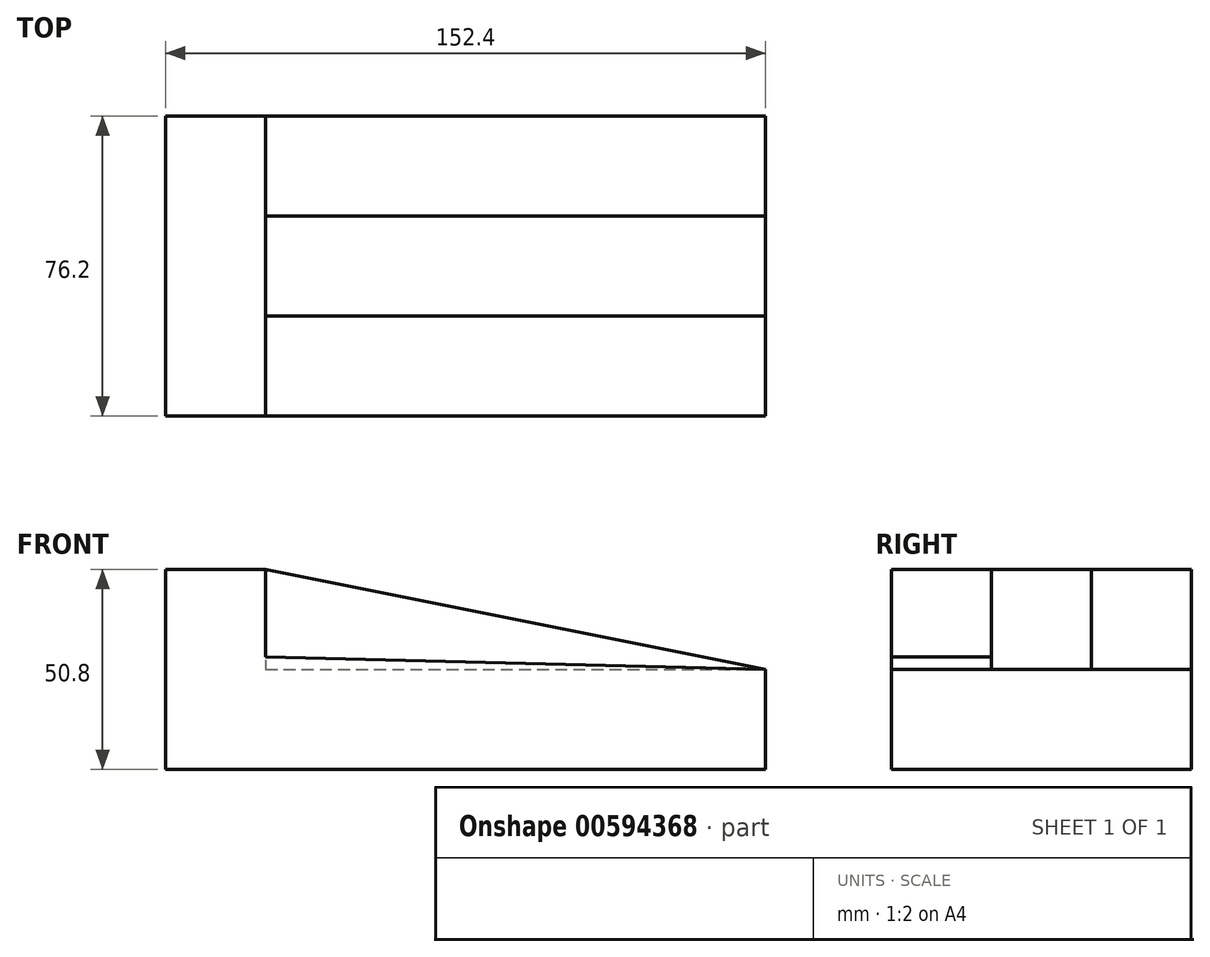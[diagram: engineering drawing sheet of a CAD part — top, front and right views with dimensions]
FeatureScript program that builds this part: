
annotation { "Feature Type Name" : "Feature", "Feature Type Description" : "" }
export const myFeature = defineFeature(function(context is Context, id is Id, definition is map)
    precondition{}
    {
        {
            var Q0;
            Q0=qCreatedBy(makeId("Front.planeOp"),FACE);
            var sketch = newSketch(context, id + "F0", { "sketchPlane" : qUnion([Q0])});
            skLineSegment(sketch, "E0", {"start": v(0, 0) * mm, "end": v(0, 50.8) * mm});
            skLineSegment(sketch, "E1", {"start": v(0, 50.8) * mm, "end": v(25.4, 50.8) * mm});
            skLineSegment(sketch, "E2", {"start": v(25.4, 50.8) * mm, "end": v(25.4, 25.4) * mm});
            skLineSegment(sketch, "E3", {"start": v(25.4, 25.4) * mm, "end": v(152.4, 25.4) * mm});
            skLineSegment(sketch, "E4", {"start": v(152.4, 25.4) * mm, "end": v(152.4, 0) * mm});
            skLineSegment(sketch, "E5", {"start": v(152.4, 0) * mm, "end": v(0, 0) * mm});
            skSolve(sketch);
        }
        {
            var Q0;
            Q0=makeQuery(id+"F0.imprint","IMPRINT",FACE,{"disambiguationData":[TD([[makeQuery(id+"F0.imprint","IMPRINT",EDGE,{"derivedFrom":sQuery(id+"F0.wireOp",EDGE,"E0")}),-1.0]])]});
            extrude(context, id + "F1", {"entities" : qUnion([Q0]), "depth" : 76.2 * mm, "offsetDistance" : 25.4 * mm});
        }
        {
            var Q0;
            Q0=makeQuery(id+"F1.opExtrude","CAP_FACE",FACE,{"disambiguationData":[OSD([sQuery(id+"F0.wireOp",EDGE,"E0"),sQuery(id+"F0.wireOp",EDGE,"E1"),sQuery(id+"F0.wireOp",EDGE,"E2"),sQuery(id+"F0.wireOp",EDGE,"E3"),sQuery(id+"F0.wireOp",EDGE,"E4"),sQuery(id+"F0.wireOp",EDGE,"E5")])],"isStart":false});
            var sketch = newSketch(context, id + "F2", { "sketchPlane" : qUnion([Q0])});
            skLineSegment(sketch, "E6", {"start": v(25.4, 50.8) * mm, "end": v(152.4, 25.4) * mm});
            skSolve(sketch);
        }
        {
            var Q0;
            Q0=makeQuery(id+"F2.imprint","IMPRINT",FACE,{"disambiguationData":[TD([[makeQuery(id+"F2.imprint","IMPRINT",EDGE,{"derivedFrom":sQuery(id+"F2.wireOp",EDGE,"E6")}),-1.0]])]});
            extrude(context, id + "F3", {"entities" : qUnion([Q0]), "operationType" : NewBodyOperationType.ADD, "oppositeDirection" : true, "depth" : 50.8 * mm, "offsetDistance" : 25.4 * mm});
        }
        {
            var Q0;
            {var subQ0=sQuery(id+"F0.wireOp",EDGE,"E3");var subQ1=sQuery(id+"F0.wireOp",EDGE,"E2");Q0=makeQuery(id+"F3.boolean.opBoolean","MERGE",FACE,{"derivedFrom":[makeQuery(id+"F1.opExtrude","CAP_FACE",FACE,{"disambiguationData":[OSD([sQuery(id+"F0.wireOp",EDGE,"E0"),sQuery(id+"F0.wireOp",EDGE,"E1"),subQ1,subQ0,sQuery(id+"F0.wireOp",EDGE,"E4"),sQuery(id+"F0.wireOp",EDGE,"E5")])],"isStart":false}),makeQuery(id+"F3.opExtrude","CAP_FACE",FACE,{"disambiguationData":[OSD([subQ1,subQ0,sQuery(id+"F2.wireOp",EDGE,"E6")])],"isStart":true})]});}
            var sketch = newSketch(context, id + "F4", { "sketchPlane" : qUnion([Q0])});
            skLineSegment(sketch, "E7", {"start": v(25.4, 50.8) * mm, "end": v(152.4, 25.4) * mm});
            skLineSegment(sketch, "E8", {"start": v(152.4, 25.4) * mm, "end": v(25.4, 28.61) * mm});
            skLineSegment(sketch, "E9", {"start": v(25.4, 28.61) * mm, "end": v(25.4, 50.8) * mm});
            skSolve(sketch);
        }
        {
            var Q0;
            Q0=makeQuery(id+"F4.imprint","IMPRINT",FACE,{"disambiguationData":[TD([[makeQuery(id+"F4.imprint","IMPRINT",EDGE,{"derivedFrom":sQuery(id+"F4.wireOp",EDGE,"E7")}),-1.0]])]});
            extrude(context, id + "F5", {"entities" : qUnion([Q0]), "operationType" : NewBodyOperationType.REMOVE, "oppositeDirection" : true, "depth" : 25.4 * mm, "offsetDistance" : 25.4 * mm});
        }
    });
